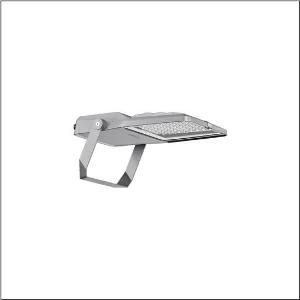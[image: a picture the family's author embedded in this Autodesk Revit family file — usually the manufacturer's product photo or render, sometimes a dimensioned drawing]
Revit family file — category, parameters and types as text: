
# Revit family: floodlight_fl_21_iq_mini___rs12_5xa7772b2b1a_75ed
name_source: partatom
category: Lighting Fixtures
units: mm (PartAtom-declared; Revit-internal decimal feet)

## family parameters
Cut with Voids When Loaded = No
Host = Face
Light Source = No
Part Type = Normal
Room Calculation Point = No
Round Connector Dimension = Use Diameter
Shared = No

## types (1)
- --- (1 x LED, 6300 lm, 45.5 W, 3000K)
    Apparent Load = 46 VA
    CIE Flux Codes = 79 92 99 100 100
    Color Rendering = 70
    Color Temperature = 3000K
    Default Elevation = 1800 mm
    Description = Floodlight FL 21 iQ mini, floodlight, primary light control with lens, of PMMA, primary optical cover: protective disc, of toughened safety glass, transparent, light distribution: RS12, light emission: direct distribution, installation type: surface-mounted, LED, High Power LED, rated luminous flux: 6.300lm, luminous efficacy: 139lm/W, light colour: 730, colour temperature: 3000K, control: Street-Remote, Auto-Match, Temp-Guard, Night-Set, Smart-Wire, Desk-Remote (wireless, voltage-free reading and setting of iQ features in the workshop via application-optimized NFC function/RFID function), optimised constant luminous flux control (CLO 2.0), with terminal, 6-pole, mains connection: 220..240V, AC, 50/60Hz, start of lifetime: 46W, end of service life: 48W, reduction: 22W, luminaire housing, of diecast aluminium, powder-coated, Siteco® metallic grey (DB 702S), corrosivity category C5 mid according to DIN EN ISO 12944, sealing non-destructively replaceable, mounting bracket, of steel, galvanised, powder-coated, Siteco® metallic grey (DB 702S), protection rating (complete): IP66, insulation class (complete): insulation class II (safety insulation), certification: CE, ENEC, VDE, protection symbol: D, impact resistance: IK08, permissible operating ambient temperature: -40..+40°C, permissible operating ambient temperature for outdoor applications: -40..+50°C, standard: DIN EN 12944, LABS conformity tested according to VDMA 24364:2018-05, packaging unit: 1 piece

Light Distribution: RS12
    Height = 70 mm
    Lamp = 1 x LED
    Lamp Light Flux = 6300 lm
    Lamp Power = 45.5 W
    Lamp count = 1
    Length = 485 mm
    Luminous efficacy = 138 lm/W
    Manufacturer = Siteco
    ModVariant = No
    Model = 5XA7772B2B1A
    Number of Poles = 1
    OnlyDefault = Yes
    Power Factor = 1
    Product Name = Floodlight FL 21 iQ mini | RS12
    Product group = floodlight | pylon annexe
    ProductGroupID = 6200
    Protection Class = Protection class II
    Protection Degree = IP 66
    RLX_Detail_Level = 1
    RLX_Emergency_Light_Flux = 0 lm
    RLX_Emergency_Type = 0
    RLX_Emergency_Type_DB = No
    RlxData = <blob elided: 90809 chars, md5=28ca29eb>
    Socket = socket
    Standby Power = 0 W
    System Light Flux = 6300 lm
    System Power = 46 W
    Type Comments = factory setting: luminous flux: 100 % | dim-lin: 254 | 463 mA
    Type Image = l_1006845.jpg
    URL = http://relux.com
    VarID = @adj_100203
    Voltage = 0 V
    Weight = 0.00 kg
    Width = 337 mm

## geometry (parser evidence)
native form markers: Blend x4, Sweep x13
no freeform markers — native parametric forms only
